# Revit family: Electronics_Masking-Generators_Biamp_Qt-Patient-Privacy-System_Control-Module
name_source: partatom
category: Communication Devices
units: mm (PartAtom-declared; Revit-internal decimal feet)

## family parameters
Cut with Voids When Loaded = No
Host = Face
Maintain Annotation Orientation = No
OmniClass Number = 23.85.10.00
OmniClass Title = General Information Systems
Part Type = Normal
Room Calculation Point = No
Round Connector Dimension = Use Diameter
Shared = No

## types (1)
- Control Module
    Apparent Load = 7 VA
    Connector Description = 100-240 VAC, 50/60 Hz
    Connector Type = Captive Screw Terminals
    Current = 1 A
    Default Elevation = 48 "
    Depth = 4 "
    Description = QT® Patient Privacy System for Waiting Rooms, Exam Rooms, and Pharmacies
    Height = 1 "
    Housing Material = Biamp - Plastic - White
    Input Connector Type = Captive Screw Terminals
    Input Impedance = 5kΩ
    Input Level = +4dBu (2VRMS max)
    Input Level Adjustment = 1dB steps
    Input Type = Contact Closure (Normally Open)
    Manufacturer = Biamp
    Masking Level Adjustment = 0.5dB steps
    Masking Ramp Times = 0-120 seconds (up and down ramp times are independent)
    Max Power Consumption = 7 W
    Maximum Masking SPL (@ 1m) = 60dBA
    Maximum Music/Paging SPL (@ 1m) = 62dBA
    Minimum Masking SPL (@ 1m) = 30dBA
    Minimum Output Impedance = 7Ω (per channel)
    Model = Control Module
    Music/Paging = 200Hz to 10kHz
    Number of Connectors = 2
    Number of Inputs = 1 (Stereo or Mono)
    Number of Masking Zones = 1 (2 cable runs per zone)
    Number of Non-Correlated Masking Sources = 4
    Number of Poles = 1
    Output Connections = 2 RJ-45
    Output Type = Logic Status (5VDC
    Output Voltage = 5VDC @ 75mA
    Power Factor = 1
    Product Documentation Link = https://downloads.biamp.com
    Product Page URL = https://www.biamp.com
    Product data url = https://bimobject.com
    Sound Masking = 200Hz to 6.3kHz
    URL = https://www.biamp.com
    Version = 1
    Voltage = 120 V
    Weight = 0.71 lb
    Width = 8 "

## geometry (parser evidence)
native form markers: Sweep x2
no freeform markers — native parametric forms only
